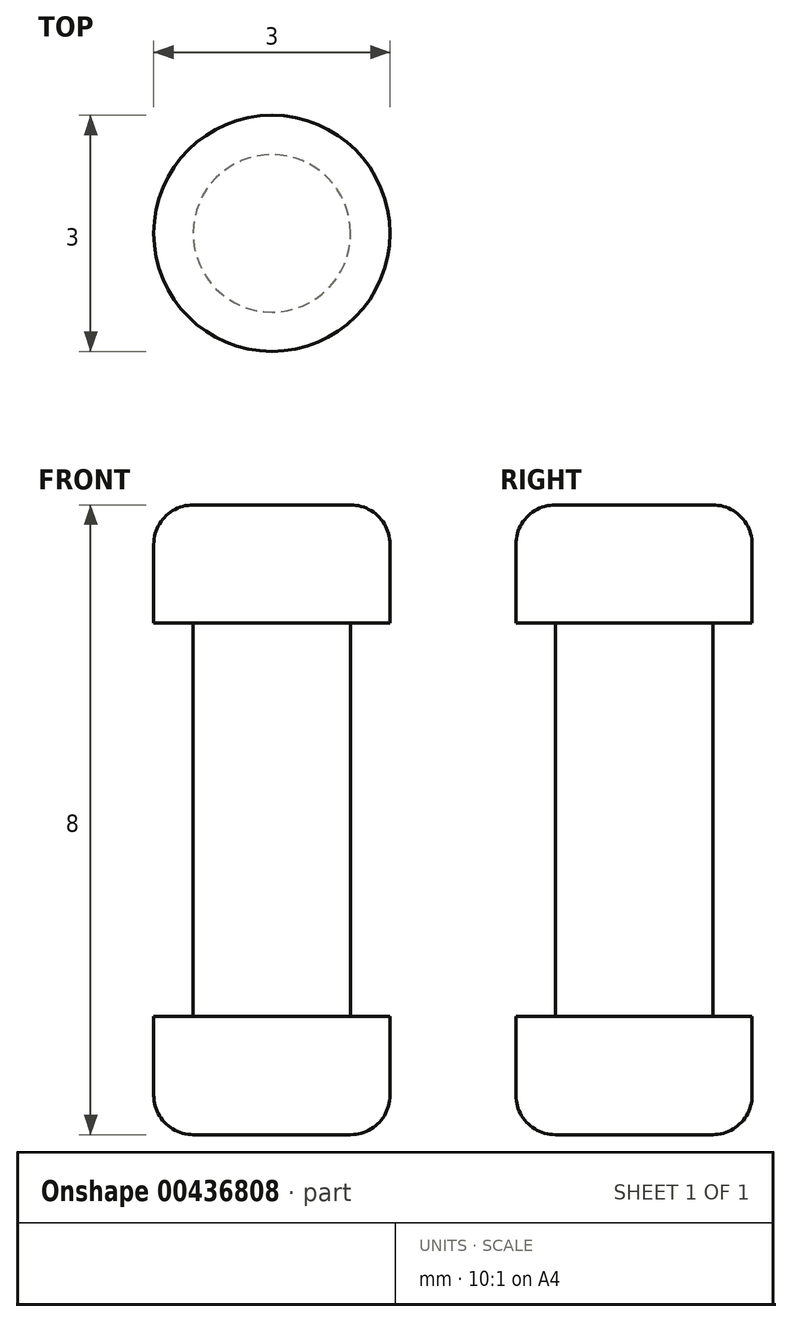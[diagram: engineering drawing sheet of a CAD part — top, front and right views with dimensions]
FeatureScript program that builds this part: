
annotation { "Feature Type Name" : "Feature", "Feature Type Description" : "" }
export const myFeature = defineFeature(function(context is Context, id is Id, definition is map)
    precondition{}
    {
        {
            var Q0;
            Q0=qCreatedBy(makeId("Top.planeOp"),FACE);
            var sketch = newSketch(context, id + "F0", { "sketchPlane" : qUnion([Q0])});
            skCircle(sketch, "E0", {"center": v(0, 0) * mm, "radius": 1 * mm});
            skSolve(sketch);
        }
        {
            var Q0;
            Q0=makeQuery(id+"F0.imprint","IMPRINT",FACE,{"disambiguationData":[TD([[makeQuery(id+"F0.imprint","IMPRINT",EDGE,{"derivedFrom":sQuery(id+"F0.wireOp",EDGE,"E0")}),1.0]])]});
            extrude(context, id + "F1", {"entities" : qUnion([Q0]), "oppositeDirection" : true, "depth" : 5 * mm});
        }
        {
            var Q0;
            Q0=makeQuery(id+"F1.opExtrude","CAP_FACE",FACE,{"disambiguationData":[OSD([sQuery(id+"F0.wireOp",EDGE,"E0")])],"isStart":true});
            var sketch = newSketch(context, id + "F2", { "sketchPlane" : qUnion([Q0])});
            skCircle(sketch, "E1", {"center": v(0, 0) * mm, "radius": 1.5 * mm});
            skSolve(sketch);
        }
        {
            var Q0;
            Q0 = qSketchRegion(id + "F2", true);
            extrude(context, id + "F3", {"entities" : qUnion([Q0]), "operationType" : NewBodyOperationType.ADD, "depth" : 1.5 * mm});
        }
        {
            var Q0;
            Q0=makeQuery(id+"F3.opExtrude","CAP_EDGE",EDGE,{"disambiguationData":[OSD([sQuery(id+"F2.wireOp",EDGE,"E1")])],"isStart":false});
            fillet(context, id + "F4", {"entities" : qUnion([Q0]), "radius" : 0.5 * mm, "tangentPropagation" : true, "allowEdgeOverflow" : false});
        }
        {
            var Q0;
            Q0=makeQuery(id+"F1.opExtrude","CAP_FACE",FACE,{"disambiguationData":[OSD([sQuery(id+"F0.wireOp",EDGE,"E0")])],"isStart":false});
            var sketch = newSketch(context, id + "F5", { "sketchPlane" : qUnion([Q0])});
            skCircle(sketch, "E2", {"center": v(0, 0) * mm, "radius": 1.5 * mm});
            skSolve(sketch);
        }
        {
            var Q0;
            Q0=makeQuery(id+"F5.imprint","IMPRINT",FACE,{"disambiguationData":[TD([[makeQuery(id+"F5.imprint","IMPRINT",EDGE,{"derivedFrom":sQuery(id+"F5.wireOp",EDGE,"E2")}),1.0]])]});
            var Q1;
            Q1=makeQuery(id+"F5.imprint","IMPRINT",FACE,{"disambiguationData":[TD([[makeQuery(id+"F5.imprint","IMPRINT",EDGE,{"derivedFrom":makeQuery(id+"F1.opExtrude","CAP_EDGE",EDGE,{"disambiguationData":[OSD([sQuery(id+"F0.wireOp",EDGE,"E0")])],"isStart":false})}),-1.0]])]});
            extrude(context, id + "F6", {"entities" : qUnion([Q0, Q1]), "operationType" : NewBodyOperationType.ADD, "depth" : 1.5 * mm});
        }
        {
            var Q0;
            Q0=makeQuery(id+"F6.opExtrude","CAP_EDGE",EDGE,{"disambiguationData":[OSD([sQuery(id+"F5.wireOp",EDGE,"E2")])],"isStart":false});
            fillet(context, id + "F7", {"entities" : qUnion([Q0]), "radius" : 0.5 * mm, "tangentPropagation" : true, "allowEdgeOverflow" : false});
        }
    });
